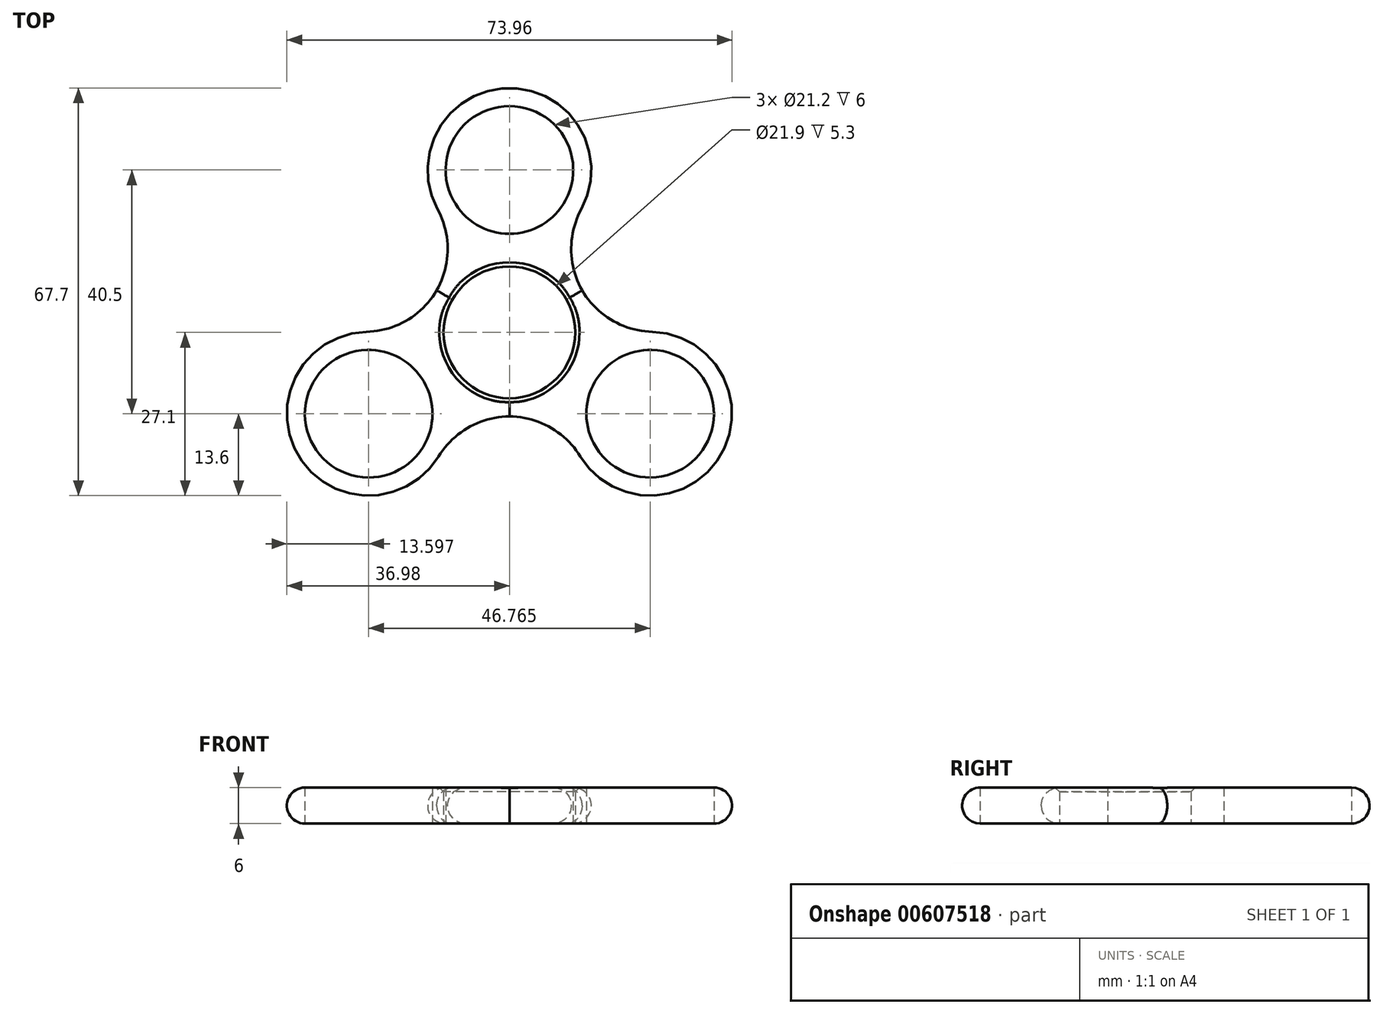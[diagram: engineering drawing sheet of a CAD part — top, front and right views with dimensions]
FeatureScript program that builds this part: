
annotation { "Feature Type Name" : "Feature", "Feature Type Description" : "" }
export const myFeature = defineFeature(function(context is Context, id is Id, definition is map)
    precondition{}
    {
        {
            var Q0;
            Q0=qCreatedBy(makeId("Top.planeOp"),FACE);
            var sketch = newSketch(context, id + "F0", { "sketchPlane" : qUnion([Q0])});
            skCircle(sketch, "E0", {"center": v(0, 0) * mm, "radius": 10.95 * mm});
            skCircle(sketch, "E1.cCircle", {"center": v(0, 0) * mm, "radius": 13.5 * mm, "construction": true});
            skLineSegment(sketch, "E1.0", {"start": v(-23.38, -13.5) * mm, "end": v(0, 27) * mm, "construction": true});
            skLineSegment(sketch, "E1.1", {"start": v(0, 27) * mm, "end": v(23.38, -13.5) * mm, "construction": true});
            skLineSegment(sketch, "E1.2", {"start": v(23.38, -13.5) * mm, "end": v(-23.38, -13.5) * mm, "construction": true});
            skPoint(sketch, "E1.0.midPoint", {"position": v(-11.7, 6.75) * mm});
            skCircle(sketch, "E2", {"center": v(0, 27) * mm, "radius": 10.6 * mm});
            skCircle(sketch, "E3", {"center": v(23.38, -13.5) * mm, "radius": 10.6 * mm});
            skCircle(sketch, "E4", {"center": v(-23.38, -13.5) * mm, "radius": 10.6 * mm});
            skCircle(sketch, "E5.0", {"center": v(-23.38, -13.5) * mm, "radius": 13.6 * mm});
            skCircle(sketch, "E6.0", {"center": v(23.38, -13.5) * mm, "radius": 13.6 * mm});
            skCircle(sketch, "E7.0", {"center": v(0, 27) * mm, "radius": 13.6 * mm});
            skCircle(sketch, "E8.0", {"center": v(0, 0) * mm, "radius": 13.95 * mm});
            skSolve(sketch);
        }
        {
            var Q0;
            Q0=qSketchRegion(id+"F0",true);
            extrude(context, id + "F1", {"entities" : qUnion([Q0]), "depth" : 6 * mm, "offsetDistance" : 25 * mm});
        }
        {
            var Q0;
            {var subQ0=sQuery(id+"F0.wireOp",EDGE,"E8.0");var subQ1=sQuery(id+"F0.wireOp",EDGE,"E5.0");Q0=makeQuery(id+"F1.opExtrude","SWEPT_EDGE",EDGE,{"disambiguationData":[OSD([subQ1,subQ0]),TDD([makeQuery(id+"F0.imprint","INTERSECT",VERTEX,{"disambiguationData":[OD(1.0)],"derivedFrom":[subQ1,subQ0]})])]});}
            var Q1;
            {var subQ0=sQuery(id+"F0.wireOp",EDGE,"E8.0");var subQ1=sQuery(id+"F0.wireOp",EDGE,"E6.0");Q1=makeQuery(id+"F1.opExtrude","SWEPT_EDGE",EDGE,{"disambiguationData":[OSD([subQ1,subQ0]),TDD([makeQuery(id+"F0.imprint","INTERSECT",VERTEX,{"disambiguationData":[OD(0.0)],"derivedFrom":[subQ1,subQ0]})])]});}
            var Q2;
            {var subQ0=sQuery(id+"F0.wireOp",EDGE,"E8.0");var subQ1=sQuery(id+"F0.wireOp",EDGE,"E7.0");Q2=makeQuery(id+"F1.opExtrude","SWEPT_EDGE",EDGE,{"disambiguationData":[OSD([subQ1,subQ0]),TDD([makeQuery(id+"F0.imprint","INTERSECT",VERTEX,{"disambiguationData":[OD(1.0)],"derivedFrom":[subQ1,subQ0]})])]});}
            var Q3;
            {var subQ0=sQuery(id+"F0.wireOp",EDGE,"E8.0");var subQ1=sQuery(id+"F0.wireOp",EDGE,"E6.0");Q3=makeQuery(id+"F1.opExtrude","SWEPT_EDGE",EDGE,{"disambiguationData":[OSD([subQ1,subQ0]),TDD([makeQuery(id+"F0.imprint","INTERSECT",VERTEX,{"disambiguationData":[OD(1.0)],"derivedFrom":[subQ1,subQ0]})])]});}
            var Q4;
            {var subQ0=sQuery(id+"F0.wireOp",EDGE,"E8.0");var subQ1=sQuery(id+"F0.wireOp",EDGE,"E7.0");Q4=makeQuery(id+"F1.opExtrude","SWEPT_EDGE",EDGE,{"disambiguationData":[OSD([subQ1,subQ0]),TDD([makeQuery(id+"F0.imprint","INTERSECT",VERTEX,{"disambiguationData":[OD(0.0)],"derivedFrom":[subQ1,subQ0]})])]});}
            var Q5;
            {var subQ0=sQuery(id+"F0.wireOp",EDGE,"E8.0");var subQ1=sQuery(id+"F0.wireOp",EDGE,"E5.0");Q5=makeQuery(id+"F1.opExtrude","SWEPT_EDGE",EDGE,{"disambiguationData":[OSD([subQ1,subQ0]),TDD([makeQuery(id+"F0.imprint","INTERSECT",VERTEX,{"disambiguationData":[OD(0.0)],"derivedFrom":[subQ1,subQ0]})])]});}
            fillet(context, id + "F2", {"entities" : qUnion([Q0, Q1, Q2, Q3, Q4, Q5]), "radius" : 14 * mm, "tangentPropagation" : true, "allowEdgeOverflow" : false});
        }
        {
            var Q0;
            Q0=makeQuery(id+"F1.opExtrude","CAP_EDGE",EDGE,{"disambiguationData":[OSD([sQuery(id+"F0.wireOp",EDGE,"E7.0")])],"isStart":false});
            var Q1;
            Q1=makeQuery(id+"F1.opExtrude","CAP_EDGE",EDGE,{"disambiguationData":[OSD([sQuery(id+"F0.wireOp",EDGE,"E7.0")])],"isStart":true});
            var Q2;
            Q2=makeQuery(id+"F1.opExtrude","CAP_EDGE",EDGE,{"disambiguationData":[OSD([sQuery(id+"F0.wireOp",EDGE,"E5.0")])],"isStart":false});
            var Q3;
            Q3=makeQuery(id+"F1.opExtrude","CAP_EDGE",EDGE,{"disambiguationData":[OSD([sQuery(id+"F0.wireOp",EDGE,"E5.0")])],"isStart":true});
            var Q4;
            Q4=makeQuery(id+"F1.opExtrude","CAP_EDGE",EDGE,{"disambiguationData":[OSD([sQuery(id+"F0.wireOp",EDGE,"E6.0")])],"isStart":false});
            var Q5;
            Q5=makeQuery(id+"F1.opExtrude","CAP_EDGE",EDGE,{"disambiguationData":[OSD([sQuery(id+"F0.wireOp",EDGE,"E6.0")])],"isStart":true});
            fillet(context, id + "F3", {"entities" : qUnion([Q0, Q1, Q2, Q3, Q4, Q5]), "radius" : 3 * mm, "tangentPropagation" : true, "allowEdgeOverflow" : false});
        }
        {
            var Q0;
            Q0=makeQuery(id+"F1.opExtrude","CAP_EDGE",EDGE,{"disambiguationData":[OSD([sQuery(id+"F0.wireOp",EDGE,"E0")])],"isStart":false});
            chamfer(context, id + "F4", {"entities" : qUnion([Q0]), "width" : .7 * mm, "tangentPropagation" : true});
        }
    });
